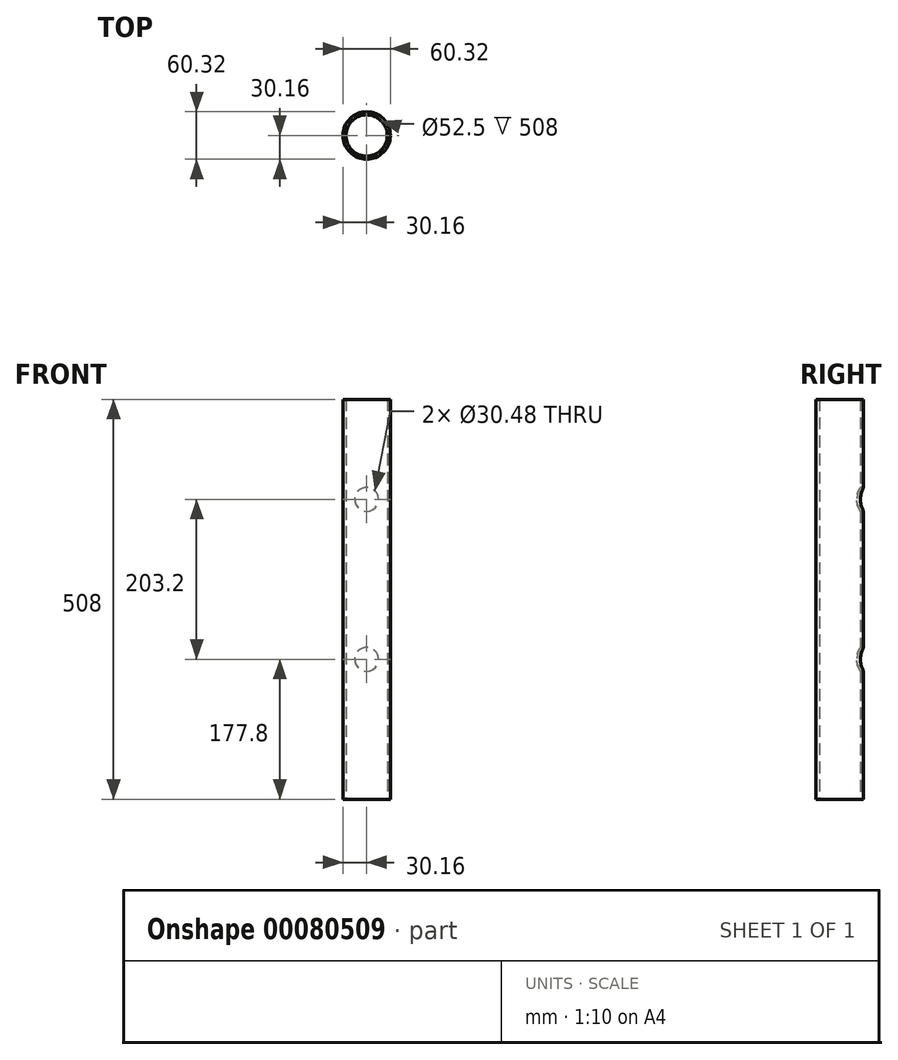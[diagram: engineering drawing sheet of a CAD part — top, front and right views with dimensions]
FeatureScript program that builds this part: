
annotation { "Feature Type Name" : "Feature", "Feature Type Description" : "" }
export const myFeature = defineFeature(function(context is Context, id is Id, definition is map)
    precondition{}
    {
        {
            var Q0;
            Q0=qCreatedBy(makeId("Top.planeOp"),FACE);
            var sketch = newSketch(context, id + "F0", { "sketchPlane" : qUnion([Q0])});
            skCircle(sketch, "E0", {"center": v(0, 0) * mm, "radius": 26.25 * mm});
            skCircle(sketch, "E1", {"center": v(0, 0) * mm, "radius": 30.16 * mm});
            skSolve(sketch);
        }
        {
            var Q0;
            Q0=makeQuery(id+"F0.imprint","IMPRINT",FACE,{"disambiguationData":[TD([[makeQuery(id+"F0.imprint","IMPRINT",EDGE,{"derivedFrom":sQuery(id+"F0.wireOp",EDGE,"E0")}),-1.0]])]});
            extrude(context, id + "F1", {"entities" : qUnion([Q0]), "depth" : 508 * mm});
        }
        {
            var Q0;
            Q0=qCreatedBy(makeId("Front.planeOp"),FACE);
            var sketch = newSketch(context, id + "F2", { "sketchPlane" : qUnion([Q0])});
            skCircle(sketch, "E2", {"center": v(0, 381) * mm, "radius": 15.24 * mm});
            skSolve(sketch);
        }
        {
            var Q0;
            Q0=qCreatedBy(makeId("Front.planeOp"),FACE);
            var sketch = newSketch(context, id + "F3", { "sketchPlane" : qUnion([Q0])});
            skCircle(sketch, "E3", {"center": v(0, 177.8) * mm, "radius": 15.24 * mm});
            skSolve(sketch);
        }
        {
            var Q0;
            Q0 = qSketchRegion(id + "F2", true);
            extrude(context, id + "F4", {"entities" : qUnion([Q0]), "operationType" : NewBodyOperationType.REMOVE, "oppositeDirection" : true, "depth" : 106.83 * mm});
        }
        {
            var Q0;
            Q0 = qSketchRegion(id + "F3", true);
            extrude(context, id + "F5", {"entities" : qUnion([Q0]), "operationType" : NewBodyOperationType.REMOVE, "oppositeDirection" : true, "depth" : 102.8 * mm});
        }
    });
